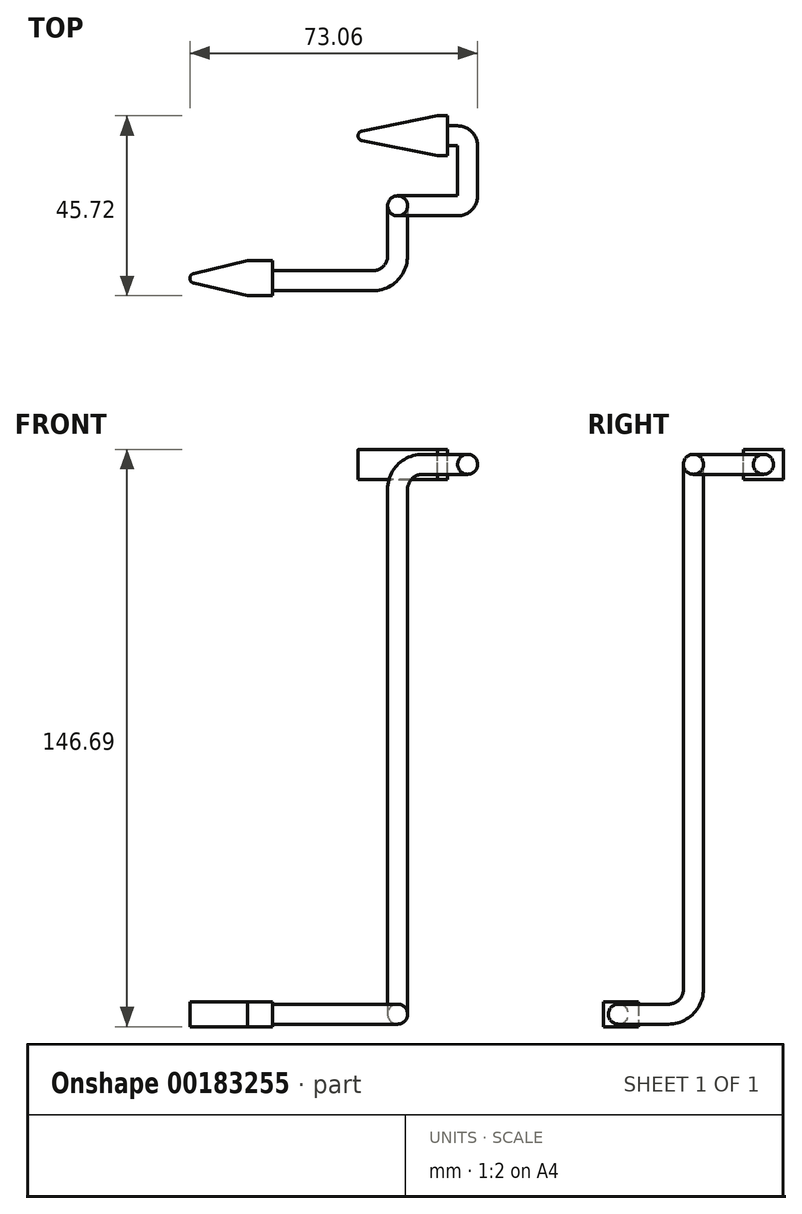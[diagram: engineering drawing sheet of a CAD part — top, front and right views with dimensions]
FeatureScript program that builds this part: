
annotation { "Feature Type Name" : "Feature", "Feature Type Description" : "" }
export const myFeature = defineFeature(function(context is Context, id is Id, definition is map)
    precondition{}
    {
        {
            var Q0;
            Q0=qCreatedBy(makeId("Right.planeOp"),FACE);
            var sketch = newSketch(context, id + "F0", { "sketchPlane" : qUnion([Q0])});
            skCircle(sketch, "E0", {"center": v(0, 0) * mm, "radius": 2.54 * mm});
            skSolve(sketch);
        }
        {
            var Q0;
            Q0=qCreatedBy(makeId("Top.planeOp"),FACE);
            var sketch = newSketch(context, id + "F1", { "sketchPlane" : qUnion([Q0])});
            skLineSegment(sketch, "E1", {"start": v(0, 0) * mm, "end": v(2.54, 0) * mm});
            skLineSegment(sketch, "E2", {"start": v(2.54, 0) * mm, "end": v(2.54, -64.55) * mm, "construction": true});
            skArc(sketch, "E3", {"start": v(5.08, -2.54) * mm, "mid": v(4.34, -0.74) * mm, "end": v(2.54, 0) * mm});
            skLineSegment(sketch, "E4", {"start": v(5.08, -2.54) * mm, "end": v(5.08, -15.24) * mm});
            skArc(sketch, "E5", {"start": v(2.54, -17.78) * mm, "mid": v(4.34, -17.04) * mm, "end": v(5.08, -15.24) * mm});
            skLineSegment(sketch, "E6", {"start": v(2.54, -17.78) * mm, "end": v(0, -17.78) * mm});
            skPoint(sketch, "E7.center.orphan", {"position": v(0, -20.32) * mm});
            skLineSegment(sketch, "E8", {"start": v(0, -17.78) * mm, "end": v(-6.35, -17.78) * mm});
            skSolve(sketch);
        }
        {
            var Q0;
            Q0=makeQuery(id+"F0.imprint","IMPRINT",FACE,{"disambiguationData":[TD([[makeQuery(id+"F0.imprint","IMPRINT",EDGE,{"derivedFrom":sQuery(id+"F0.wireOp",EDGE,"E0")}),1.0]])]});
            var Q1;
            Q1=sQuery(id+"F1.wireOp",EDGE,"E1");
            var Q2;
            Q2=sQuery(id+"F1.wireOp",EDGE,"E3");
            var Q3;
            Q3=sQuery(id+"F1.wireOp",EDGE,"E4");
            var Q4;
            Q4=sQuery(id+"F1.wireOp",EDGE,"E5");
            var Q5;
            Q5=sQuery(id+"F1.wireOp",EDGE,"E6");
            var Q6;
            Q6=sQuery(id+"F1.wireOp",EDGE,"E8");
            sweep(context, id + "F2", {"profiles" : qUnion([Q0]), "path" : qUnion([Q1, Q2, Q3, Q4, Q5, Q6])});
        }
        {
            var Q0;
            Q0=qCreatedBy(makeId("Top.planeOp"),FACE);
            var sketch = newSketch(context, id + "F3", { "sketchPlane" : qUnion([Q0])});
            skLineSegment(sketch, "E9.bottom", {"start": v(0, 5.08) * mm, "end": v(-2.54, 5.08) * mm});
            skLineSegment(sketch, "E9.top", {"start": v(0, -5.08) * mm, "end": v(-2.54, -5.08) * mm});
            skLineSegment(sketch, "E9.left", {"start": v(0, 5.08) * mm, "end": v(0, -5.08) * mm});
            skLineSegment(sketch, "E9.right", {"start": v(-2.54, 5.08) * mm, "end": v(-2.54, -5.08) * mm});
            skSolve(sketch);
        }
        {
            var Q0;
            Q0=makeQuery(id+"F3.imprint","IMPRINT",FACE,{"disambiguationData":[TD([[makeQuery(id+"F3.imprint","IMPRINT",EDGE,{"derivedFrom":sQuery(id+"F3.wireOp",EDGE,"E9.bottom")}),1.0]])]});
            extrude(context, id + "F4", {"entities" : qUnion([Q0]), "operationType" : NewBodyOperationType.ADD, "endBound" : BoundingType.SYMMETRIC, "oppositeDirection" : true, "depth" : 7.62 * mm});
        }
        {
            var Q0;
            Q0=makeQuery(id+"F4.opExtrude","CAP_FACE",FACE,{"disambiguationData":[OSD([sQuery(id+"F3.wireOp",EDGE,"E9.bottom"),sQuery(id+"F3.wireOp",EDGE,"E9.top"),sQuery(id+"F3.wireOp",EDGE,"E9.left"),sQuery(id+"F3.wireOp",EDGE,"E9.right")])],"isStart":true});
            var sketch = newSketch(context, id + "F5", { "sketchPlane" : qUnion([Q0])});
            skLineSegment(sketch, "E10", {"start": v(-2.54, 5.08) * mm, "end": v(-27.94, 0) * mm});
            skLineSegment(sketch, "E11", {"start": v(-27.94, 0) * mm, "end": v(-2.54, -5.08) * mm});
            skLineSegment(sketch, "E12", {"start": v(-2.54, -5.08) * mm, "end": v(-2.54, 5.08) * mm});
            skSolve(sketch);
        }
        {
            var Q0;
            Q0=makeQuery(id+"F5.imprint","IMPRINT",FACE,{"disambiguationData":[TD([[makeQuery(id+"F5.imprint","IMPRINT",EDGE,{"derivedFrom":sQuery(id+"F5.wireOp",EDGE,"E10")}),1.0]])]});
            var Q1;
            Q1=makeQuery(id+"F4.opExtrude","CAP_FACE",FACE,{"disambiguationData":[OSD([sQuery(id+"F3.wireOp",EDGE,"E9.bottom"),sQuery(id+"F3.wireOp",EDGE,"E9.top"),sQuery(id+"F3.wireOp",EDGE,"E9.left"),sQuery(id+"F3.wireOp",EDGE,"E9.right")])],"isStart":false});
            extrude(context, id + "F6", {"entities" : qUnion([Q0]), "operationType" : NewBodyOperationType.ADD, "endBound" : BoundingType.UP_TO_SURFACE, "oppositeDirection" : true, "endBoundEntityFace" : qUnion([Q1]), "depth" : 25.4 * mm});
        }
        {
            var Q0;
            Q0=makeQuery(id+"F6.opExtrude","SWEPT_EDGE",EDGE,{"disambiguationData":[OSD([sQuery(id+"F5.wireOp",EDGE,"E10"),sQuery(id+"F5.wireOp",EDGE,"E11")])]});
            fillet(context, id + "F7", {"entities" : qUnion([Q0]), "radius" : 1.27 * mm, "tangentPropagation" : true, "allowEdgeOverflow" : false});
        }
        {
            var Q0;
            Q0=makeQuery(id+"F4.opExtrude","SWEPT_FACE",FACE,{"disambiguationData":[OSD([sQuery(id+"F3.wireOp",EDGE,"E9.top")])]});
            var sketch = newSketch(context, id + "F8", { "sketchPlane" : qUnion([Q0])});
            skLineSegment(sketch, "E13", {"start": v(-37.22, 0) * mm, "end": v(-46.26, 3.53) * mm});
            skLineSegment(sketch, "E14", {"start": v(-37.22, 0) * mm, "end": v(-46.26, -3.1) * mm});
            skLineSegment(sketch, "E15", {"start": v(-46.26, -3.1) * mm, "end": v(-46.26, 3.53) * mm});
            skSolve(sketch);
        }
        {
            var Q0;
            Q0=makeQuery(id+"F8.imprint","IMPRINT",FACE,{"disambiguationData":[TD([[makeQuery(id+"F8.imprint","IMPRINT",EDGE,{"derivedFrom":sQuery(id+"F8.wireOp",EDGE,"E13")}),1.0]])]});
            extrude(context, id + "F9", {"entities" : qUnion([Q0]), "operationType" : NewBodyOperationType.REMOVE, "oppositeDirection" : true, "depth" : 25.4 * mm});
        }
        {
            var Q0;
            Q0=qCreatedBy(makeId("Front.planeOp"),FACE);
            var sketch = newSketch(context, id + "F10", { "sketchPlane" : qUnion([Q0])});
            skLineSegment(sketch, "E16", {"start": v(0, 0) * mm, "end": v(-31.33, 0) * mm, "construction": true});
            skArc(sketch, "E17", {"start": v(-6.35, 0) * mm, "mid": v(-10.84, -1.86) * mm, "end": v(-12.7, -6.35) * mm});
            skLineSegment(sketch, "E18", {"start": v(-6.35, -6.35) * mm, "end": v(-6.35, 13.13) * mm, "construction": true});
            skLineSegment(sketch, "E19", {"start": v(-12.7, -6.35) * mm, "end": v(-12.7, -133.35) * mm});
            skSolve(sketch);
        }
        {
            var Q0;
            Q0=makeQuery(id+"F2.opSweep","CAP_FACE",FACE,{"disambiguationData":[OSD([sQuery(id+"F0.wireOp",EDGE,"E0"),sQuery(id+"F1.wireOp",VERTEX,"E8.end")])],"isStart":false});
            var Q1;
            Q1=sQuery(id+"F10.wireOp",EDGE,"E17");
            var Q2;
            Q2=sQuery(id+"F10.wireOp",EDGE,"E19");
            sweep(context, id + "F11", {"operationType" : NewBodyOperationType.ADD, "profiles" : qUnion([Q0]), "path" : qUnion([Q1, Q2])});
        }
        {
            var Q0;
            Q0=qCreatedBy(makeId("Right.planeOp"),FACE);
            var sketch = newSketch(context, id + "F12", { "sketchPlane" : qUnion([Q0])});
            skLineSegment(sketch, "E20", {"start": v(0, 0) * mm, "end": v(0, 10.2) * mm, "construction": true});
            skLineSegment(sketch, "E21.0", {"start": v(-15.24, -133.35) * mm, "end": v(-20.32, -133.35) * mm});
            skLineSegment(sketch, "E22", {"start": v(-20.32, -133.35) * mm, "end": v(-64.15, -133.35) * mm, "construction": true});
            skPoint(sketch, "E23", {"position": v(-17.78, -133.35) * mm});
            skArc(sketch, "E24", {"start": v(-24.13, -139.7) * mm, "mid": v(-19.64, -137.84) * mm, "end": v(-17.78, -133.35) * mm});
            skLineSegment(sketch, "E25", {"start": v(-24.13, -139.7) * mm, "end": v(-30.48, -139.7) * mm});
            skSolve(sketch);
        }
        {
            var Q0;
            Q0=makeQuery(id+"F11.opSweep","CAP_FACE",FACE,{"disambiguationData":[OSD([sQuery(id+"F0.wireOp",EDGE,"E0"),sQuery(id+"F1.wireOp",VERTEX,"E8.end"),sQuery(id+"F10.wireOp",VERTEX,"E19.end")])],"isStart":false});
            var Q1;
            Q1=sQuery(id+"F12.wireOp",EDGE,"E24");
            var Q2;
            Q2=sQuery(id+"F12.wireOp",EDGE,"E25");
            sweep(context, id + "F13", {"operationType" : NewBodyOperationType.ADD, "profiles" : qUnion([Q0]), "path" : qUnion([Q1, Q2])});
        }
        {
            var Q0;
            Q0=qCreatedBy(makeId("Top.planeOp"),FACE);
            var sketch = newSketch(context, id + "F14", { "sketchPlane" : qUnion([Q0])});
            skLineSegment(sketch, "E26.0", {"start": v(-10.16, -30.48) * mm, "end": v(-15.24, -30.48) * mm});
            skPoint(sketch, "E27", {"position": v(-12.7, -30.48) * mm});
            skArc(sketch, "E28", {"start": v(-19.05, -36.83) * mm, "mid": v(-14.56, -34.97) * mm, "end": v(-12.7, -30.48) * mm});
            skLineSegment(sketch, "E29", {"start": v(-19.05, -36.83) * mm, "end": v(-44.45, -36.83) * mm});
            skSolve(sketch);
        }
        {
            var Q0;
            Q0=makeQuery(id+"F13.opSweep","CAP_FACE",FACE,{"disambiguationData":[OSD([sQuery(id+"F0.wireOp",EDGE,"E0"),sQuery(id+"F1.wireOp",VERTEX,"E8.end"),sQuery(id+"F10.wireOp",VERTEX,"E19.end"),sQuery(id+"F12.wireOp",VERTEX,"E25.end")])],"isStart":false});
            var Q1;
            Q1=sQuery(id+"F14.wireOp",EDGE,"E28");
            var Q2;
            Q2=sQuery(id+"F14.wireOp",EDGE,"E29");
            sweep(context, id + "F15", {"operationType" : NewBodyOperationType.ADD, "profiles" : qUnion([Q0]), "path" : qUnion([Q1, Q2])});
        }
        {
            var Q0;
            Q0=qCreatedBy(makeId("Top.planeOp"),FACE);
            cPlane(context, id + "F16", {"entities" : qUnion([Q0]), "cplaneType" : CPlaneType.OFFSET, "offset" : 139.7 * mm, "oppositeDirection" : true, "width" : 152.4 * mm, "height" : 152.4 * mm});
        }
        {
            var Q0;
            Q0=qCreatedBy(id+"F16.planeOp",FACE);
            var sketch = newSketch(context, id + "F17", { "sketchPlane" : qUnion([Q0])});
            skLineSegment(sketch, "E30.0", {"start": v(-44.45, -39.37) * mm, "end": v(-44.45, -34.3) * mm});
            skLineSegment(sketch, "E31.bottom", {"start": v(-44.45, -31.75) * mm, "end": v(-50.8, -31.75) * mm});
            skLineSegment(sketch, "E31.top", {"start": v(-44.45, -40.64) * mm, "end": v(-50.8, -40.64) * mm});
            skLineSegment(sketch, "E31.left", {"start": v(-44.45, -31.75) * mm, "end": v(-44.45, -40.64) * mm});
            skLineSegment(sketch, "E32", {"start": v(-50.8, -31.75) * mm, "end": v(-69.73, -36.2) * mm});
            skLineSegment(sketch, "E33", {"start": v(-69.73, -36.2) * mm, "end": v(-50.8, -40.64) * mm});
            skSolve(sketch);
        }
        {
            var Q0;
            {var subQ1=sQuery(id+"F17.wireOp",EDGE,"E31.bottom");Q0=makeQuery(id+"F17.imprint","IMPRINT",FACE,{"disambiguationData":[TD([[makeQuery(id+"F17.imprint","IMPRINT",EDGE,{"derivedFrom":subQ1}),1.0]])]});}
            extrude(context, id + "F18", {"entities" : qUnion([Q0]), "operationType" : NewBodyOperationType.ADD, "endBound" : BoundingType.SYMMETRIC, "depth" : 6.35 * mm});
        }
        {
            var Q0;
            Q0=makeQuery(id+"F18.opExtrude","SWEPT_EDGE",EDGE,{"disambiguationData":[OSD([sQuery(id+"F17.wireOp",EDGE,"E32"),sQuery(id+"F17.wireOp",EDGE,"E33")])]});
            fillet(context, id + "F19", {"entities" : qUnion([Q0]), "radius" : 1.27 * mm, "tangentPropagation" : true, "allowEdgeOverflow" : false});
        }
    });
